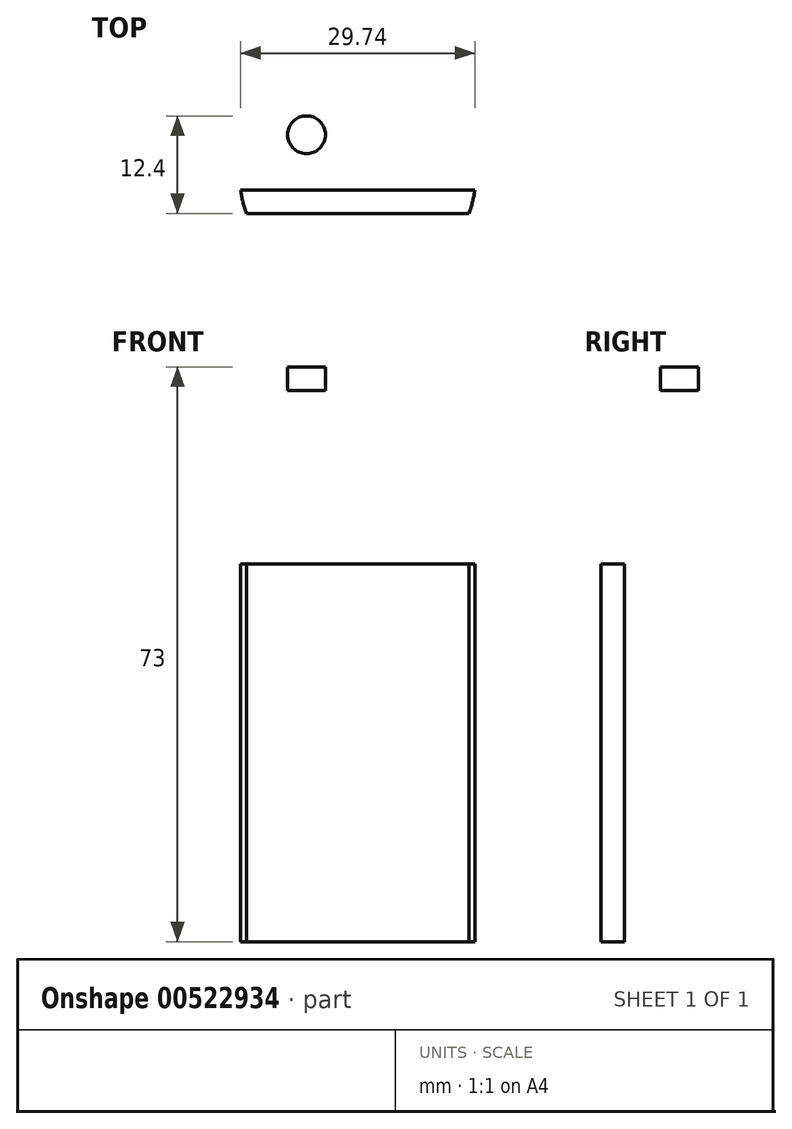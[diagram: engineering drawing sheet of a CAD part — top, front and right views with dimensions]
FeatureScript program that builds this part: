
annotation { "Feature Type Name" : "Feature", "Feature Type Description" : "" }
export const myFeature = defineFeature(function(context is Context, id is Id, definition is map)
    precondition{}
    {
        {
            var Q0;
            Q0=qCreatedBy(makeId("Top.planeOp"),FACE);
            var sketch = newSketch(context, id + "F0", { "sketchPlane" : qUnion([Q0])});
            skCircle(sketch, "E0", {"center": v(0, 0) * mm, "radius": 15 * mm});
            skSolve(sketch);
        }
        {
            var Q0;
            Q0=makeQuery(id+"F0.imprint","IMPRINT",FACE,{"disambiguationData":[TD([[makeQuery(id+"F0.imprint","IMPRINT",EDGE,{"derivedFrom":sQuery(id+"F0.wireOp",EDGE,"E0")}),1.0]])]});
            extrude(context, id + "F1", {"entities" : qUnion([Q0]), "depth" : 3 * mm, "offsetDistance" : 25 * mm});
        }
        {
            var Q0;
            Q0=qCreatedBy(makeId("Top.planeOp"),FACE);
            var sketch = newSketch(context, id + "F2", { "sketchPlane" : qUnion([Q0])});
            skLineSegment(sketch, "E1.bottom", {"start": v(14.87, -2) * mm, "end": v(-14.87, -2) * mm});
            skLineSegment(sketch, "E1.top", {"start": v(14.14, -5) * mm, "end": v(-14.14, -5) * mm});
            skPoint(sketch, "E1.middle", {"position": v(0, 0) * mm});
            skCircle(sketch, "E2", {"center": v(0, 0) * mm, "radius": 15 * mm});
            skPoint(sketch, "E3.orphan", {"position": v(-15.2, -5) * mm});
            skPoint(sketch, "E4.orphan", {"position": v(-15.2, 5) * mm});
            skPoint(sketch, "E1.left.end.orphan", {"position": v(15.2, -5) * mm});
            skPoint(sketch, "E5.orphan", {"position": v(15.2, 5) * mm});
            skSolve(sketch);
        }
        {
            var Q0;
            Q0=makeQuery(id+"F2.imprint","IMPRINT",FACE,{"disambiguationData":[TD([[makeQuery(id+"F2.imprint","IMPRINT",EDGE,{"derivedFrom":sQuery(id+"F2.wireOp",EDGE,"E1.bottom")}),1.0]])]});
            extrude(context, id + "F3", {"entities" : qUnion([Q0]), "operationType" : NewBodyOperationType.ADD, "oppositeDirection" : true, "depth" : 70 * mm, "offsetDistance" : 25 * mm});
        }
        {
            var Q0;
            {var subQ0=sQuery(id+"F0.wireOp",EDGE,"E0");var subQ1=sQuery(id+"F2.wireOp",EDGE,"E1.top");Q0=makeQuery(id+"F3.boolean.opBoolean","SPLIT",FACE,{"disambiguationData":[TD([makeQuery(id+"F3.opExtrude","SWEPT_FACE",FACE,{"disambiguationData":[OSD([subQ1])]})])],"derivedFrom":makeQuery(id+"F1.opExtrude","CAP_FACE",FACE,{"disambiguationData":[OSD([subQ0])],"isStart":true})});}
            var sketch = newSketch(context, id + "F4", { "sketchPlane" : qUnion([Q0])});
            skLineSegment(sketch, "E6", {"start": v(-12.29, 8.6) * mm, "end": v(12.29, 8.6) * mm, "construction": true});
            skPoint(sketch, "E7", {"position": v(0, 10.6) * mm});
            skLineSegment(sketch, "E8.bottom", {"start": v(-4, 8.6) * mm, "end": v(4, 8.6) * mm});
            skLineSegment(sketch, "E8.top", {"start": v(-4, 12.6) * mm, "end": v(4, 12.6) * mm});
            skLineSegment(sketch, "E8.left", {"start": v(-4, 8.6) * mm, "end": v(-4, 12.6) * mm});
            skLineSegment(sketch, "E8.right", {"start": v(4, 8.6) * mm, "end": v(4, 12.6) * mm});
            skSolve(sketch);
        }
        {
            var Q0;
            Q0=makeQuery(id+"F4.imprint","IMPRINT",FACE,{"disambiguationData":[TD([[makeQuery(id+"F4.imprint","IMPRINT",EDGE,{"derivedFrom":sQuery(id+"F4.wireOp",EDGE,"E8.bottom")}),1.0]])]});
            extrude(context, id + "F5", {"entities" : qUnion([Q0]), "operationType" : NewBodyOperationType.REMOVE, "oppositeDirection" : true, "depth" : 25 * mm, "offsetDistance" : 25 * mm});
        }
        {
            var Q0;
            Q0=makeQuery(id+"F1.opExtrude","CAP_FACE",FACE,{"disambiguationData":[OSD([sQuery(id+"F0.wireOp",EDGE,"E0")])],"isStart":false});
            var sketch = newSketch(context, id + "F6", { "sketchPlane" : qUnion([Q0])});
            skLineSegment(sketch, "E9", {"start": v(0, 0) * mm, "end": v(0, 15) * mm, "construction": true});
            skPoint(sketch, "E10", {"position": v(6.5, 5) * mm});
            skCircle(sketch, "E11", {"center": v(6.5, 5) * mm, "radius": 2.4 * mm});
            skCircle(sketch, "E12.MirrorC", {"center": v(-6.5, 5) * mm, "radius": 2.4 * mm});
            skSolve(sketch);
        }
        {
            var Q0;
            Q0=makeQuery(id+"F6.imprint","IMPRINT",FACE,{"disambiguationData":[TD([[makeQuery(id+"F6.imprint","IMPRINT",EDGE,{"derivedFrom":sQuery(id+"F6.wireOp",EDGE,"E12.MirrorC")}),-1.0]])]});
            var Q1;
            Q1=makeQuery(id+"F6.imprint","IMPRINT",FACE,{"disambiguationData":[TD([[makeQuery(id+"F6.imprint","IMPRINT",EDGE,{"derivedFrom":sQuery(id+"F6.wireOp",EDGE,"E11")}),1.0]])]});
            extrude(context, id + "F7", {"entities" : qUnion([Q0, Q1]), "operationType" : NewBodyOperationType.REMOVE, "oppositeDirection" : true, "depth" : 25 * mm, "offsetDistance" : 25 * mm});
        }
    });
